# Revit family: CENTUM Wandwinkel 2-Loch XL100
name_source: partatom
category: HLS-Bauteile
units: mm (PartAtom-declared; Revit-internal decimal feet)

## family parameters
Arbeitsebenenbasiert = Ja
Beim Laden mit Abzugskörper schneiden = Nein
Bemaßung runder Anschluss = Durchmesser verwenden
Beschriftungsausrichtung beibehalten = Nein
Gemeinsam genutzt = Ja
Immer vertikal = Nein
Raumberechnungspunkt = Nein
Teiletyp = Normal

## types (1)
- CENTUM Wandwinkel 2-Loch XL100
    Artikelnummer = 1640101005
    Breite Material = 90 mm  [stored 0.295276 ft]
    EAN = 4250928468116
    Fabrikat = MEFA
    Firma = MEFA Befestigungs- und Montagesysteme GmbH
    Gewicht = 1.29 kg
    Gewicht pro Bauteil = 1.29 kg
    Kurztext1 = CENTUM Wandwinkel 2-Loch
    Kurztext2 = 90 ° Schenkel 95 x 95 mm
    Langloch = 14x40 mm
    Lochdurchmesser = 14 mm  [stored 0.0459318 ft]
    Länge Schenkel 1 = 95 mm
    Länge Schenkel 2 = 95 mm
    Material = Stahl
    Materialname = S235
    Mengeneinheit = St
    Profil = CENTUM
    Profiltyp = XL 100, XL 120
    Sicherheitsfaktor = 1.54
    Stärke Material = 10 mm  [stored 0.0328084 ft]
    Vorgabe-Ansicht = 1219 mm
    Winkel = 90 °
    vpe = 1

note: [stored X ft] marks values corroborated as IEEE doubles in the binary element streams (Revit-internal decimal feet)
